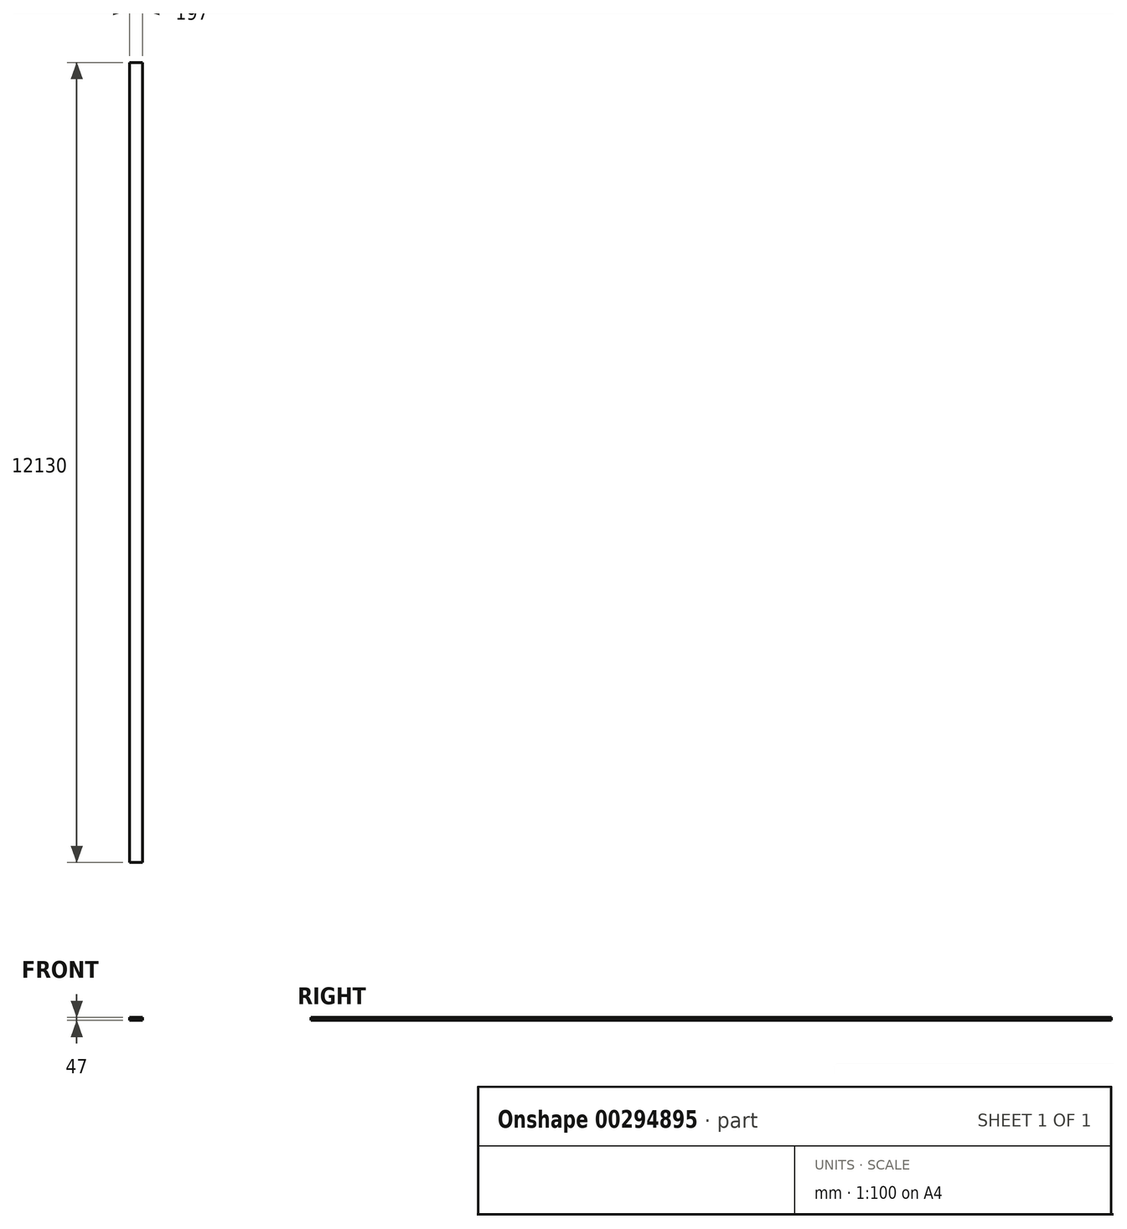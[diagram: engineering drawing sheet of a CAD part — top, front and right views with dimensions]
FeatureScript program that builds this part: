
annotation { "Feature Type Name" : "Feature", "Feature Type Description" : "" }
export const myFeature = defineFeature(function(context is Context, id is Id, definition is map)
    precondition{}
    {
        {
            var Q0;
            Q0=qCreatedBy(makeId("Front.planeOp"),FACE);
            var sketch = newSketch(context, id + "F0", { "sketchPlane" : qUnion([Q0])});
            skLineSegment(sketch, "E0.bottom", {"start": v(98.5, 23.5) * mm, "end": v(-98.5, 23.5) * mm});
            skLineSegment(sketch, "E0.top", {"start": v(98.5, -23.5) * mm, "end": v(-98.5, -23.5) * mm});
            skLineSegment(sketch, "E0.left", {"start": v(98.5, 23.5) * mm, "end": v(98.5, -23.5) * mm});
            skLineSegment(sketch, "E0.right", {"start": v(-98.5, 23.5) * mm, "end": v(-98.5, -23.5) * mm});
            skPoint(sketch, "E0.middle", {"position": v(0, 0) * mm});
            skSolve(sketch);
        }
        {
            var Q0;
            Q0=makeQuery(id+"F0.imprint","IMPRINT",FACE,{"disambiguationData":[TD([[makeQuery(id+"F0.imprint","IMPRINT",EDGE,{"derivedFrom":sQuery(id+"F0.wireOp",EDGE,"E0.bottom")}),1.0]])]});
            extrude(context, id + "F1", {"entities" : qUnion([Q0]), "depth" : 12130 * mm});
        }
    });
